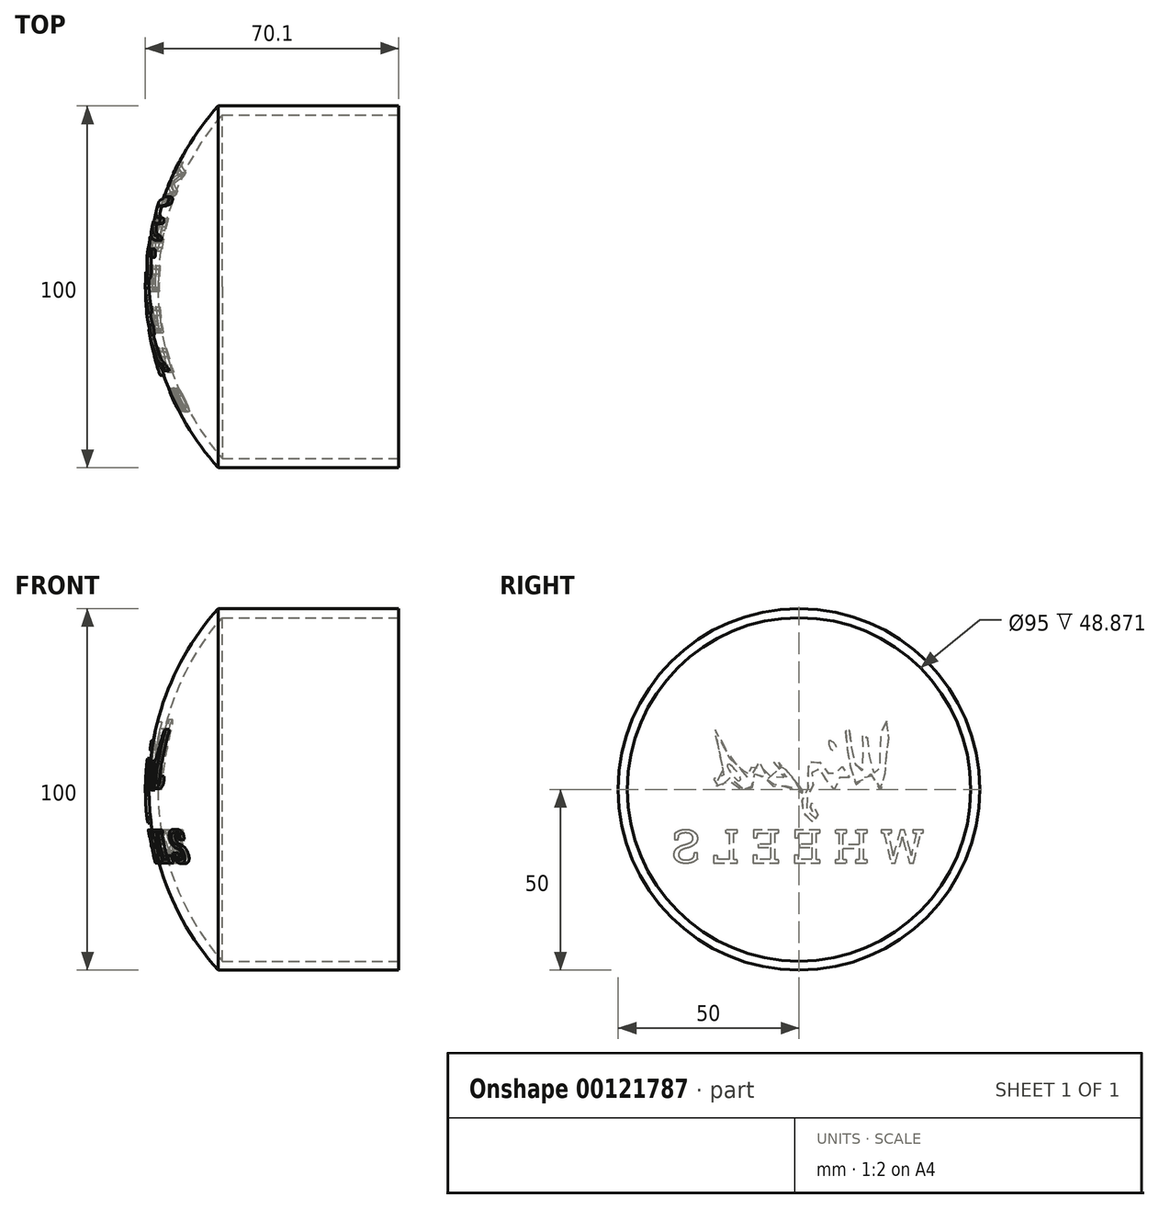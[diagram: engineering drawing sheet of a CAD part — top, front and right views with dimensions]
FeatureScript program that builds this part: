
annotation { "Feature Type Name" : "Feature", "Feature Type Description" : "" }
export const myFeature = defineFeature(function(context is Context, id is Id, definition is map)
    precondition{}
    {
        {
            var Q0;
            Q0=qCreatedBy(makeId("Front.planeOp"),FACE);
            var sketch = newSketch(context, id + "F0", { "sketchPlane" : qUnion([Q0])});
            skLineSegment(sketch, "E0", {"start": v(0, 50) * mm, "end": v(-50, 50) * mm});
            skLineSegment(sketch, "E1", {"start": v(0, 0) * mm, "end": v(0, 50) * mm});
            skArc(sketch, "E2", {"start": v(-50, 50) * mm, "mid": v(-64.16, 26.76) * mm, "end": v(-69.1, 0) * mm});
            skLineSegment(sketch, "E3", {"start": v(0, 0) * mm, "end": v(-96.64, 0) * mm, "construction": true});
            skLineSegment(sketch, "E4", {"start": v(-69.1, 0) * mm, "end": v(0, 0) * mm});
            skLineSegment(sketch, "E5", {"start": v(0, 0) * mm, "end": v(0, -46.86) * mm, "construction": true});
            skLineSegment(sketch, "E6", {"start": v(0, 0) * mm, "end": v(46.17, 0) * mm, "construction": true});
            skLineSegment(sketch, "E7", {"start": v(0, 0) * mm, "end": v(0, 59.8) * mm, "construction": true});
            skSolve(sketch);
        }
        {
            var Q0;
            Q0=qSketchRegion(id+"F0",true);
            var Q1;
            Q1=sQuery(id+"F0.wireOp",EDGE,"E3");
            revolve(context, id + "F1", {"entities" : qUnion([Q0]), "axis" : qUnion([Q1]), "revolveType" : RevolveType.FULL});
        }
        {
            var Q0;
            Q0=makeQuery(id+"F1.opRevolve","SWEPT_FACE",FACE,{"disambiguationData":[OSD([sQuery(id+"F0.wireOp",EDGE,"E1")])]});
            shell(context, id + "F2", {"entities" : qUnion([Q0]), "thickness" : 2.5 * mm});
        }
        {
            var Q0;
            Q0=qCreatedBy(makeId("Front.planeOp"),FACE);
            var sketch = newSketch(context, id + "F3", { "sketchPlane" : qUnion([Q0])});
            skArc(sketch, "E8.0", {"start": v(-50.75, 50.67) * mm, "mid": v(-65.1, 27.12) * mm, "end": v(-70.1, 0) * mm});
            skSolve(sketch);
        }
        {
            var Q0;
            Q0=qSketchRegion(id+"F3",true);
            var Q1;
            Q1=sQuery(id+"F3.wireOp",EDGE,"E8.0");
            var Q2;
            Q2=sQuery(id+"F0.wireOp",EDGE,"E3");
            revolve(context, id + "F4", {"bodyType" : ToolBodyType.SURFACE, "entities" : qUnion([Q0]), "surfaceEntities" : qUnion([Q1]), "axis" : qUnion([Q2]), "revolveType" : RevolveType.FULL});
        }
        {
            var Q0;
            Q0=sQuery(id+"F0.wireOp",EDGE,"E7");
            cPlane(context, id + "F5", {"entities" : qUnion([Q0]), "cplaneType" : CPlaneType.LINE_ANGLE, "offset" : 150 * mm, "angle" : 180 * degree, "width" : 150 * mm, "height" : 150 * mm});
        }
        {
            var Q0;
            Q0=qCreatedBy(id+"F5.planeOp",FACE);
            cPlane(context, id + "F6", {"entities" : qUnion([Q0]), "cplaneType" : CPlaneType.OFFSET, "offset" : 75 * mm, "width" : 150 * mm, "height" : 150 * mm});
        }
        {
            var Q0;
            Q0=sQuery(id+"F0.wireOp",EDGE,"E1");
            cPlane(context, id + "F7", {"entities" : qUnion([Q0]), "cplaneType" : CPlaneType.LINE_ANGLE, "offset" : 75 * mm, "angle" : 180 * degree, "width" : 150 * mm, "height" : 150 * mm});
        }
        {
            var Q0;
            Q0=qCreatedBy(id+"F7.planeOp",FACE);
            var sketch = newSketch(context, id + "F8", { "sketchPlane" : qUnion([Q0])});
            skText(sketch, "E9", { "text": "W H E E L S", "fontName": "RobotoSlab-Regular.ttf"});
            skLineSegment(sketch, "E10", {"start": v(0, 0) * mm, "end": v(0, 58.78) * mm, "construction": true});
            skLineSegment(sketch, "E11", {"start": v(0, 0) * mm, "end": v(-62.43, 0) * mm, "construction": true});
            skLineSegment(sketch, "E12", {"start": v(-35.9, -0.04) * mm, "end": v(34.3, -0.04) * mm, "construction": true});
            skFitSpline(sketch, "E13", {"points": [v(-24.29, 18.93) * mm, v(-24.65, 11.36) * mm, v(-24.34, 10.41) * mm, v(-22.58, -0.04) * mm, v(-18.85, 5.76) * mm, v(-17.8, 1.34) * mm, v(-16.06, 0.93) * mm, v(-13.07, 18.52) * mm, v(-13.64, 18.3) * mm, v(-14.15, 14.59) * mm, v(-16.84, 3.9) * mm, v(-17.63, 10.37) * mm, v(-17.8, 16.71) * mm, v(-18.69, 15.97) * mm, v(-19.34, 10.05) * mm, v(-21.89, 3) * mm, v(-23.13, 18.75) * mm, v(-24.29, 18.93) * mm]});
            skFitSpline(sketch, "E14", {"points": [v(-0.75, -0.88) * mm, v(1.03, 1.33) * mm, v(1.55, -0.06) * mm, v(6.4, 2.72) * mm, v(7.31, -0.04) * mm, v(8.5, 1.11) * mm, v(11.32, 5.89) * mm, v(12.26, 5.72) * mm, v(11.99, -0.06) * mm, v(14.54, 2.49) * mm, v(14.48, 1.03) * mm, v(16.2, -0.06) * mm, v(19.05, 3.27) * mm, v(19.36, 0.8) * mm, v(22.47, 0.61) * mm, v(24.08, 1.7) * mm, v(24.28, 2.12) * mm, v(24.39, 3.6) * mm, v(23.65, 2.84) * mm, v(21.24, 1.55) * mm, v(21.44, 7.36) * mm, v(23.15, 16.43) * mm, v(22.73, 16.43) * mm, v(20.02, 9.32) * mm, v(19.64, 8.9) * mm, v(16.3, 6.33) * mm, v(14.53, 3.69) * mm, v(13.02, 2.33) * mm, v(13.26, 6.29) * mm, v(11.62, 7.77) * mm, v(10.57, 7.55) * mm, v(10.5, 6.88) * mm, v(7.84, 2.2) * mm, v(7.23, 5.34) * mm, v(3.17, 2.24) * mm, v(3.17, 3.04) * mm, v(7.08, 7.57) * mm, v(6.94, 8.33) * mm, v(-1.05, -0.7) * mm, v(-0.75, -0.88) * mm]});
            skFitSpline(sketch, "E15", {"points": [v(19.34, 6.92) * mm, v(16.2, 2.95) * mm, v(16.8, 2.41) * mm, v(19.88, 6.63) * mm, v(19.34, 6.92) * mm]});
            skFitSpline(sketch, "E16", {"points": [v(-8.27, 13.38) * mm, v(-9.55, 12.91) * mm, v(-10.33, 11.14) * mm, v(-9.16, 10.86) * mm, v(-8.5, 11.68) * mm, v(-8.27, 13.38) * mm]});
            skFitSpline(sketch, "E17", {"points": [v(-13.97, 3.29) * mm, v(-11.23, 6.78) * mm, v(-10.52, 6.28) * mm, v(-9.43, 3.03) * mm, v(-7.95, 4.62) * mm, v(-4.3, 8.54) * mm, v(-2.82, 7.71) * mm, v(-2.45, 4.25) * mm, v(-3.07, 2.1) * mm, v(-1.7, -1.24) * mm, v(-0.83, -5.6) * mm, v(-3.81, -9.02) * mm, v(-5.1, -9.3) * mm, v(-5.5, -8.1) * mm, v(-2.89, -2.92) * mm, v(-2.4, -2.92) * mm, v(-4.71, -8.14) * mm, v(-1.86, -5.07) * mm, v(-4.03, 1.8) * mm, v(-3.53, 5.07) * mm, v(-4.9, 6.34) * mm, v(-9.67, -0.04) * mm, v(-11.68, 3.93) * mm, v(-13.6, 3.03) * mm, v(-13.97, 3.29) * mm]});
            const initialGuessF8  = {"E9": [-0.0346, -0.02035, 1, 0, 0.00928]};
            skSetInitialGuess(sketch, initialGuessF8);
            skSolve(sketch);
        }
        {
            var Q0;
            Q0=qSketchRegion(id+"F8",true);
            var Q1;
            Q1=makeQuery(id+"F4.opRevolve","SWEPT_FACE",FACE,{"disambiguationData":[OSD([sQuery(id+"F3.wireOp",EDGE,"E8.0")])]});
            var Q2;
            Q2=makeQuery(id+"F2.opShell","OFFSET_FACE",FACE,{"disambiguationData":[OSD([sQuery(id+"F0.wireOp",EDGE,"E2")])]});
            extrude(context, id + "F9", {"entities" : qUnion([Q0]), "operationType" : NewBodyOperationType.ADD, "endBound" : BoundingType.UP_TO_SURFACE, "endBoundEntityFace" : qUnion([Q1]), "depth" : 25 * mm, "hasSecondDirection" : true, "secondDirectionBound" : SecondDirectionBoundingType.UP_TO_SURFACE, "secondDirectionOppositeDirection" : false, "secondDirectionBoundEntityFace" : qUnion([Q2]), "secondDirectionDepth" : 25 * mm});
        }
    });
